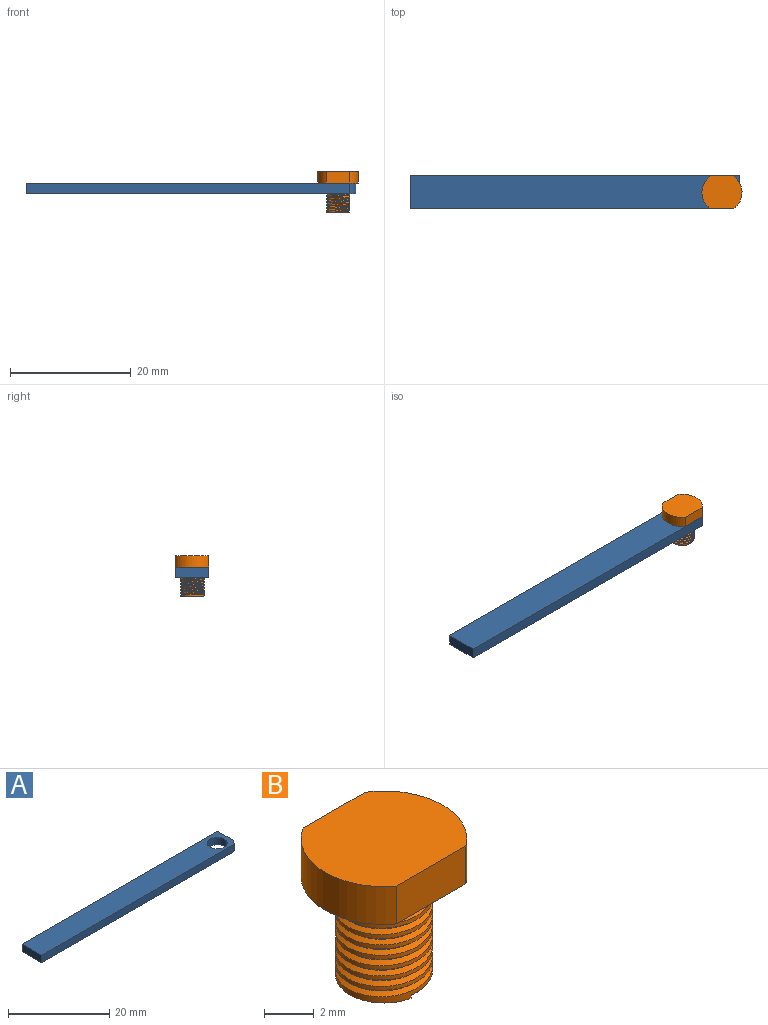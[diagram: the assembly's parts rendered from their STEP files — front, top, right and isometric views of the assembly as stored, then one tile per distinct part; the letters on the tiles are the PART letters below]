
ASSEMBLY  parts=2 mates=1
PART A: 8 faces, bbox 54.6x5.5x1.8 mm
  f0: plane 53.65x1.78mm, normal (0,-1,0), area 95.4mm2, adj f1,f4,f6,f7
  f1: cylinder r=3.32mm len=1.78mm, axis (0,0,-1), area 2.6mm2, adj f0,f2,f6,f7
  f2: plane 4.4x1.78mm, normal (1,0,0), area 7.8mm2, adj f1,f3,f6,f7
  f3: plane 54.6x1.78mm, normal (0,1,0), area 97.1mm2, adj f2,f4,f6,f7
  f4: plane 5.49x1.78mm, normal (-1,0,0), area 9.8mm2, adj f0,f3,f6,f7
  f5: cylinder r=1.94mm len=3.89mm, axis (0,0,-1), area 21.7mm2, adj f6,f7
  f6: plane 54.6x5.49mm, normal (0,0,1), area 287.5mm2, adj f0,f1,f2,f3,f4,f5
  f7: plane 54.6x5.49mm, normal (0,0,-1), area 287.5mm2, adj f0,f1,f2,f3,f4,f5
PART B: 13 faces, bbox 6.7x5.6x7 mm
  f0: cylinder r=1.94mm len=4.83mm, axis (0,0,-1), area 19.1mm2, adj f1,f2,f8,f9,f10,f11
  f1: plane 3.98x3.95mm, normal (0,0,-1), area 11.6mm2, adj f0,f8,f9
  f2: plane 6.66x5.52mm, normal (0,0,-1), area 19.8mm2, adj f0,f3,f4,f5,f6,f11,f12
  f3: cylinder r=3.32mm len=5.49mm, axis (0,0,-1), area 12mm2, adj f2,f4,f6,f7
  f4: plane 3.51x1.85mm, normal (0,1,0), area 6.5mm2, adj f2,f3,f5,f7
  f5: cylinder r=3.32mm len=5.49mm, axis (0,0,-1), area 12mm2, adj f2,f4,f6,f7
  f6: plane 3.94x1.85mm, normal (0,-1,0), area 7.3mm2, adj f2,f3,f5,f7
  f7: plane 6.64x5.49mm, normal (0,0,1), area 31.7mm2, adj f3,f4,f5,f6
  f8: plane 0.21x0.18mm, normal (1,0,0), area 0mm2, adj f0,f1,f11
  f9: bspline ~5.06x4.42mm, area 26.1mm2, adj f0,f1,f10,f11
  f10: plane 0.34x0.21mm, normal (1,0,0), area 0mm2, adj f0,f9,f11,f12
  f11: bspline ~5.08x4.42mm, area 28.5mm2, adj f0,f2,f8,f9,f10,f12
  f12: bspline ~3.2x1.83mm, area 0.4mm2, adj f2,f10,f11
PLACE A t=(-10.93,-6.93,4.92)mm fixed
PLACE B rot(axis=(0,0,-1),0deg) t=(-10.93,-6.93,4.92)mm
MATE cylindrical A.f1 <-> B.f0  axis (0,0,-1) through (20.44,-4.26,6.7)mm
